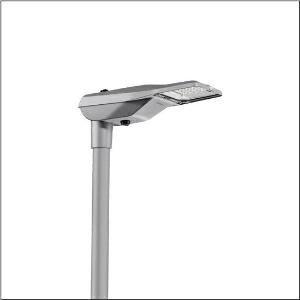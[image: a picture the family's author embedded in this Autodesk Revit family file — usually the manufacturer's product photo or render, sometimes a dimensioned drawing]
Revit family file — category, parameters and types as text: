
# Revit family: streetlight_sl_21_micro___st0_8a_5xe1c33t08db_e381
name_source: partatom
category: Lighting Fixtures
units: mm (PartAtom-declared; Revit-internal decimal feet)

## family parameters
Cut with Voids When Loaded = No
Host = Face
Light Source = No
Part Type = Normal
Room Calculation Point = No
Round Connector Dimension = Use Diameter
Shared = No

## types (1)
- --- (1 x LED, 5110 lm, 39.1 W, 3000K)
    Apparent Load = 39 VA
    CIE Flux Codes = 38 75 97 100 100
    Color Rendering = 70
    Color Temperature = 3000K
    Default Elevation = 1800 mm
    Description = Streetlight SL 21 micro, mast luminaire, primary light control with lens, of PMMA, primary optical cover: cover, of toughened safety glass, transparent, light distribution: ST0.8a, light emission: direct distribution, primary light characteristic: asymmetric, installation type: side-entry, post-top, LED, High Power LED, rated luminous flux: 5.110lm, luminous efficacy: 131lm/W, light colour: 730, colour temperature: 3000K, control: flexible luminous flux parameterisation, time-dependent luminous flux control, constant luminous flux control, overheat protection, pre-setting: logarithmic dimming characteristic, mains connection: 220..240V, AC, 50/60Hz, start of lifetime: 39W, end of service life: 41W, reduction: 18W, luminaire housing, of diecast aluminium, powder-coated, Siteco® metallic grey (DB 702S), corrosivity category C5 mid according to DIN EN ISO 12944, please order mast flange separately, inclination adjustable: 0°, 5°, 10°, 15°, sealing non-destructively replaceable, multi-level sealing system, length: 528mm, width: 235mm, height: 110mm, mast flange for spigot size: 42mm (side-entry): 5XC10008XM4, 60/48mm (side-entry/post-top): 5XC10108XM2, 76/60mm (side-entry/post-top): 5XC10108XM1, Smart Interface below and above, protection rating (complete): IP66, insulation class (complete): insulation class II (safety insulation), certification: CE, ENEC, ENEC+, VDE, impact resistance: IK09, permissible operating ambient temperature for outdoor applications: -40..+50°C, standard-compliant lighting for roads and squares, packaging unit: 1 piece

Light Distribution: ST0.8a
    Height = 110 mm
    Lamp = 1 x LED
    Lamp Light Flux = 5110 lm
    Lamp Power = 39.1 W
    Lamp count = 1
    Length = 528 mm
    Luminous efficacy = 131 lm/W
    Manufacturer = Siteco
    ModVariant = No
    Model = 5XE1C33T08DB
    Number of Poles = 1
    OnlyDefault = Yes
    Power Factor = 1
    Product Name = Streetlight SL 21 micro | ST0.8a
    Product group = mast luminaire | pylon top
    ProductGroupID = 6100
    Protection Class = Protection class II
    Protection Degree = IP 66
    RLX_Detail_Level = 1
    RLX_Emergency_Light_Flux = 0 lm
    RLX_Emergency_Type = 0
    RLX_Emergency_Type_DB = No
    RlxData = <blob elided: 98573 chars, md5=f82650aa>
    Socket = socket
    Standby Power = 0 W
    System Light Flux = 5110 lm
    System Power = 39 W
    Type Comments = factory setting: luminous flux: 100 % | dim-lin: 254 | 765 mA
    Type Image = l_1007239.jpg
    URL = http://relux.com
    VarID = @adj_124723
    Voltage = 0 V
    Weight = 0.00 kg
    Width = 235 mm

## geometry (parser evidence)
native form markers: Blend x4, Sweep x10
no freeform markers — native parametric forms only
